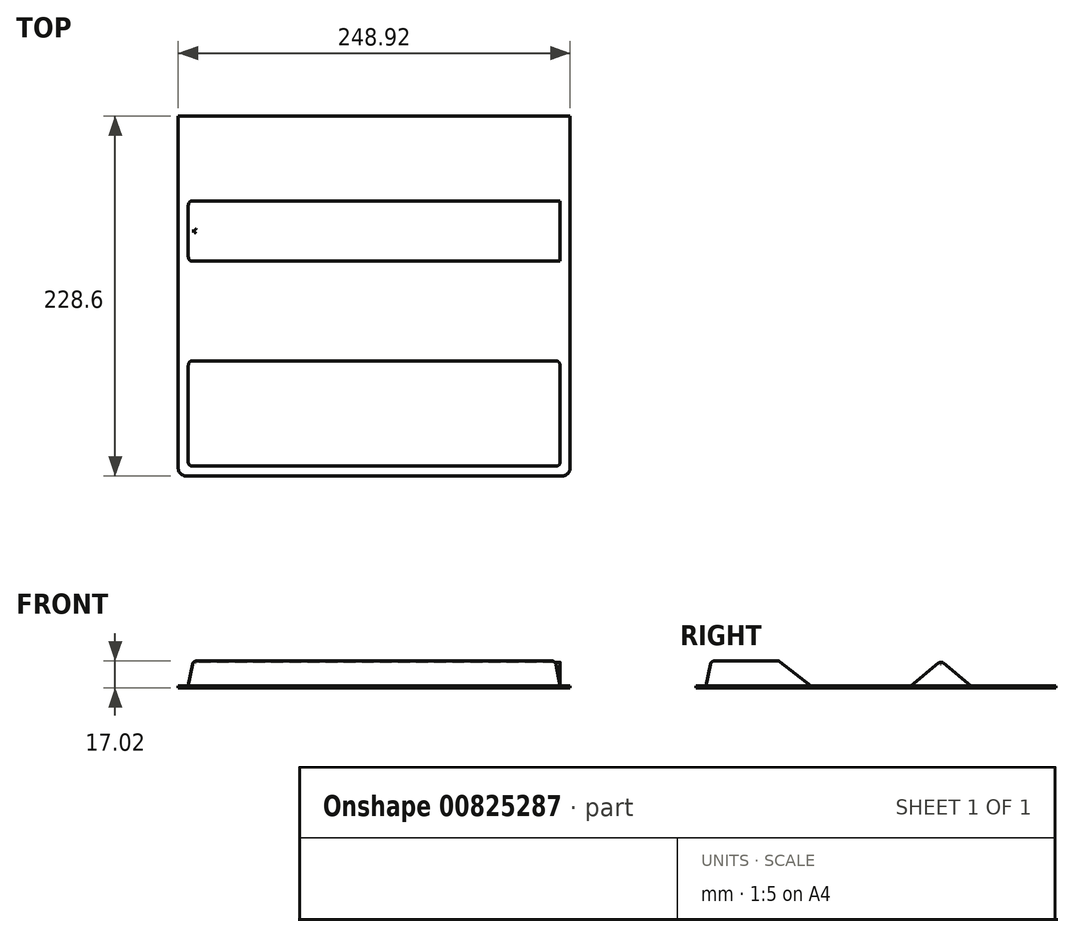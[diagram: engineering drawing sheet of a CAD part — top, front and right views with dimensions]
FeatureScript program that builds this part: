
annotation { "Feature Type Name" : "Feature", "Feature Type Description" : "" }
export const myFeature = defineFeature(function(context is Context, id is Id, definition is map)
    precondition{}
    {
        {
            var Q0;
            Q0=qCreatedBy(makeId("Top.planeOp"),FACE);
            var sketch = newSketch(context, id + "F0", { "sketchPlane" : qUnion([Q0])});
            skLineSegment(sketch, "E0.bottom", {"start": v(-124.46, -114.3) * mm, "end": v(124.46, -114.3) * mm});
            skLineSegment(sketch, "E0.top", {"start": v(-124.46, 114.3) * mm, "end": v(124.46, 114.3) * mm});
            skLineSegment(sketch, "E0.left", {"start": v(-124.46, -114.3) * mm, "end": v(-124.46, 114.3) * mm});
            skLineSegment(sketch, "E0.right", {"start": v(124.46, -114.3) * mm, "end": v(124.46, 114.3) * mm});
            skPoint(sketch, "E0.middle", {"position": v(0, 0) * mm});
            skSolve(sketch);
        }
        {
            var Q0;
            Q0=makeQuery(id+"F0.imprint","IMPRINT",FACE,{"disambiguationData":[TD([[makeQuery(id+"F0.imprint","IMPRINT",EDGE,{"derivedFrom":sQuery(id+"F0.wireOp",EDGE,"E0.bottom")}),1.0]])]});
            extrude(context, id + "F1", {"entities" : qUnion([Q0]), "depth" : 1.27 * mm, "offsetDistance" : 25.4 * mm});
        }
        {
            var Q0;
            Q0=makeQuery(id+"F1.opExtrude","CAP_FACE",FACE,{"disambiguationData":[OSD([sQuery(id+"F0.wireOp",EDGE,"E0.bottom"),sQuery(id+"F0.wireOp",EDGE,"E0.top"),sQuery(id+"F0.wireOp",EDGE,"E0.left"),sQuery(id+"F0.wireOp",EDGE,"E0.right")])],"isStart":false});
            var sketch = newSketch(context, id + "F2", { "sketchPlane" : qUnion([Q0])});
            skLineSegment(sketch, "E1.bottom", {"start": v(118.11, -107.95) * mm, "end": v(-118.11, -107.95) * mm});
            skLineSegment(sketch, "E1.top", {"start": v(118.11, -41.28) * mm, "end": v(-118.11, -41.28) * mm});
            skLineSegment(sketch, "E1.left", {"start": v(118.11, -107.95) * mm, "end": v(118.11, -41.28) * mm});
            skLineSegment(sketch, "E1.right", {"start": v(-118.11, -107.95) * mm, "end": v(-118.11, -41.28) * mm});
            skPoint(sketch, "E1.middle", {"position": v(0, -74.61) * mm});
            skSolve(sketch);
        }
        {
            var Q0;
            Q0=qCreatedBy(makeId("Top.planeOp"),FACE);
            cPlane(context, id + "F3", {"entities" : qUnion([Q0]), "cplaneType" : CPlaneType.OFFSET, "offset" : 17.02 * mm, "width" : 152.4 * mm, "height" : 152.4 * mm});
        }
        {
            var Q0;
            Q0=qCreatedBy(id+"F3.planeOp",FACE);
            var sketch = newSketch(context, id + "F4", { "sketchPlane" : qUnion([Q0])});
            skLineSegment(sketch, "E2.bottom", {"start": v(114.94, -104.78) * mm, "end": v(-114.94, -104.78) * mm});
            skLineSegment(sketch, "E2.top", {"start": v(114.94, -61.6) * mm, "end": v(-114.94, -61.6) * mm});
            skLineSegment(sketch, "E2.left", {"start": v(114.94, -104.78) * mm, "end": v(114.94, -61.6) * mm});
            skLineSegment(sketch, "E2.right", {"start": v(-114.94, -104.78) * mm, "end": v(-114.94, -61.6) * mm});
            skPoint(sketch, "E2.middle", {"position": v(0, -83.19) * mm});
            skSolve(sketch);
        }
        {
            var Q1;
            Q1=makeQuery(id+"F4.imprint","IMPRINT",FACE,{"disambiguationData":[TD([[makeQuery(id+"F4.imprint","IMPRINT",EDGE,{"derivedFrom":sQuery(id+"F4.wireOp",EDGE,"E2.bottom")}),-1.0]])]});
            var Q2;
            Q2=makeQuery(id+"F2.imprint","IMPRINT",FACE,{"disambiguationData":[TD([[makeQuery(id+"F2.imprint","IMPRINT",EDGE,{"derivedFrom":sQuery(id+"F2.wireOp",EDGE,"E1.bottom")}),-1.0]])]});
            loft(context, id + "F5", {"operationType" : NewBodyOperationType.ADD, "sheetProfilesArray" : [{ "sheetProfileEntities" : qUnion([Q1]) }, { "sheetProfileEntities" : qUnion([Q2]) }]});
        }
        {
            var Q0;
            Q0=qCreatedBy(makeId("Right.planeOp"),FACE);
            var sketch = newSketch(context, id + "F6", { "sketchPlane" : qUnion([Q0])});
            skLineSegment(sketch, "E3", {"start": v(22.22, 1.27) * mm, "end": v(60.32, 1.27) * mm});
            skLineSegment(sketch, "E4", {"start": v(60.32, 1.27) * mm, "end": v(41.27, 17.02) * mm});
            skLineSegment(sketch, "E5", {"start": v(41.27, 17.02) * mm, "end": v(22.22, 1.27) * mm});
            skSolve(sketch);
        }
        {
            var Q0;
            Q0=makeQuery(id+"F6.imprint","IMPRINT",FACE,{"disambiguationData":[TD([[makeQuery(id+"F6.imprint","IMPRINT",EDGE,{"derivedFrom":sQuery(id+"F6.wireOp",EDGE,"E3")}),1.0]])]});
            extrude(context, id + "F7", {"entities" : qUnion([Q0]), "operationType" : NewBodyOperationType.ADD, "endBound" : BoundingType.SYMMETRIC, "depth" : 236.22 * mm, "offsetDistance" : 25.4 * mm});
        }
        {
            var Q0;
            Q0=qCreatedBy(id+"F3.planeOp",FACE);
            var sketch = newSketch(context, id + "F8", { "sketchPlane" : qUnion([Q0])});
            skLineSegment(sketch, "E6.left", {"start": v(-114.94, 21.55) * mm, "end": v(-114.94, 60.52) * mm});
            skLineSegment(sketch, "E6.right", {"start": v(-118.25, 21.55) * mm, "end": v(-118.25, 60.52) * mm});
            skLineSegment(sketch, "E7", {"start": v(-118.25, 60.52) * mm, "end": v(-114.94, 60.52) * mm});
            skLineSegment(sketch, "E8", {"start": v(-118.25, 21.55) * mm, "end": v(-114.94, 21.55) * mm});
            skSolve(sketch);
        }
        {
            var Q0;
            Q0=makeQuery(id+"F2.imprint","IMPRINT",FACE,{"disambiguationData":[TD([[makeQuery(id+"F2.imprint","IMPRINT",EDGE,{"derivedFrom":sQuery(id+"F2.wireOp",EDGE,"E1.bottom")}),1.0]])]});
            var sketch = newSketch(context, id + "F9", { "sketchPlane" : qUnion([Q0])});
            skLineSegment(sketch, "E9.bottom", {"start": v(-124.68, 60.59) * mm, "end": v(-118.1, 60.59) * mm});
            skLineSegment(sketch, "E9.top", {"start": v(-124.68, 20.65) * mm, "end": v(-118.1, 20.65) * mm});
            skLineSegment(sketch, "E9.left", {"start": v(-124.68, 60.59) * mm, "end": v(-124.68, 20.65) * mm});
            skLineSegment(sketch, "E9.right", {"start": v(-118.1, 60.59) * mm, "end": v(-118.1, 20.65) * mm});
            skSolve(sketch);
        }
        {
            var Q1;
            Q1 = qSketchRegion(id + "F8", true);
            var Q2;
            Q2 = qSketchRegion(id + "F9", true);
            loft(context, id + "F10", {"operationType" : NewBodyOperationType.REMOVE, "sheetProfilesArray" : [{ "sheetProfileEntities" : qUnion([Q1]) }, { "sheetProfileEntities" : qUnion([Q2]) }]});
        }
        {
            var Q0;
            Q0=makeQuery(id+"F10.boolean.opBoolean","INTERSECT",EDGE,{"derivedFrom":[makeQuery(id+"F7.opExtrude","SWEPT_FACE",FACE,{"disambiguationData":[OSD([sQuery(id+"F6.wireOp",EDGE,"E4")])]}),makeQuery(id+"F10.opLoft","SWEPT_FACE",FACE,{"disambiguationData":[OSD([sQuery(id+"F8.wireOp",EDGE,"E6.left"),sQuery(id+"F8.wireOp",EDGE,"E7"),sQuery(id+"F8.wireOp",EDGE,"E8"),sQuery(id+"F9.wireOp",EDGE,"E9.bottom"),sQuery(id+"F9.wireOp",EDGE,"E9.top"),sQuery(id+"F9.wireOp",EDGE,"E9.right")])]})]});
            var Q1;
            Q1=makeQuery(id+"F10.boolean.opBoolean","INTERSECT",EDGE,{"derivedFrom":[makeQuery(id+"F7.opExtrude","SWEPT_FACE",FACE,{"disambiguationData":[OSD([sQuery(id+"F6.wireOp",EDGE,"E5")])]}),makeQuery(id+"F10.opLoft","SWEPT_FACE",FACE,{"disambiguationData":[OSD([sQuery(id+"F8.wireOp",EDGE,"E6.left"),sQuery(id+"F8.wireOp",EDGE,"E7"),sQuery(id+"F8.wireOp",EDGE,"E8"),sQuery(id+"F9.wireOp",EDGE,"E9.bottom"),sQuery(id+"F9.wireOp",EDGE,"E9.top"),sQuery(id+"F9.wireOp",EDGE,"E9.right")])]})]});
            var Q2;
            Q2=makeQuery(id+"F7.opExtrude","SWEPT_EDGE",EDGE,{"disambiguationData":[OSD([sQuery(id+"F6.wireOp",EDGE,"E4"),sQuery(id+"F6.wireOp",EDGE,"E5")])]});
            var Q3;
            Q3=makeQuery(id+"FepYB7Uw0ol19Tb_1.1.F10.boolean.opBoolean","INTERSECT",EDGE,{"derivedFrom":[makeQuery(id+"F7.opExtrude","SWEPT_FACE",FACE,{"disambiguationData":[OSD([sQuery(id+"F6.wireOp",EDGE,"E4")])]}),makeQuery(id+"FepYB7Uw0ol19Tb_1.1.F10.opLoft","SWEPT_FACE",FACE,{"disambiguationData":[OSD([sQuery(id+"F8.wireOp",EDGE,"E6.left"),sQuery(id+"F8.wireOp",EDGE,"E7"),sQuery(id+"F8.wireOp",EDGE,"E8"),sQuery(id+"F9.wireOp",EDGE,"E9.bottom"),sQuery(id+"F9.wireOp",EDGE,"E9.top"),sQuery(id+"F9.wireOp",EDGE,"E9.right")])]})]});
            var Q4;
            Q4=makeQuery(id+"FepYB7Uw0ol19Tb_1.1.F10.boolean.opBoolean","INTERSECT",EDGE,{"derivedFrom":[makeQuery(id+"F7.opExtrude","SWEPT_FACE",FACE,{"disambiguationData":[OSD([sQuery(id+"F6.wireOp",EDGE,"E5")])]}),makeQuery(id+"FepYB7Uw0ol19Tb_1.1.F10.opLoft","SWEPT_FACE",FACE,{"disambiguationData":[OSD([sQuery(id+"F8.wireOp",EDGE,"E6.left"),sQuery(id+"F8.wireOp",EDGE,"E7"),sQuery(id+"F8.wireOp",EDGE,"E8"),sQuery(id+"F9.wireOp",EDGE,"E9.bottom"),sQuery(id+"F9.wireOp",EDGE,"E9.top"),sQuery(id+"F9.wireOp",EDGE,"E9.right")])]})]});
            var Q5;
            Q5=makeQuery(id+"F5.opLoft","SWEPT_EDGE",EDGE,{"disambiguationData":[OSD([sQuery(id+"F2.wireOp",EDGE,"E1.top"),sQuery(id+"F2.wireOp",EDGE,"E1.right"),sQuery(id+"F4.wireOp",EDGE,"E2.top"),sQuery(id+"F4.wireOp",EDGE,"E2.right")])]});
            var Q6;
            Q6=makeQuery(id+"F5.opLoft","MID_CAP_EDGE",EDGE,{"disambiguationData":[OSD([sQuery(id+"F4.wireOp",EDGE,"E2.top"),sQuery(id+"F4.wireOp",EDGE,"E2.left"),sQuery(id+"F4.wireOp",EDGE,"E2.right")])],"capPos":0.0});
            var Q7;
            Q7=makeQuery(id+"F5.opLoft","SWEPT_EDGE",EDGE,{"disambiguationData":[OSD([sQuery(id+"F2.wireOp",EDGE,"E1.top"),sQuery(id+"F2.wireOp",EDGE,"E1.left"),sQuery(id+"F4.wireOp",EDGE,"E2.top"),sQuery(id+"F4.wireOp",EDGE,"E2.left")])]});
            var Q8;
            Q8=makeQuery(id+"F5.opLoft","MID_CAP_EDGE",EDGE,{"disambiguationData":[OSD([sQuery(id+"F4.wireOp",EDGE,"E2.bottom"),sQuery(id+"F4.wireOp",EDGE,"E2.top"),sQuery(id+"F4.wireOp",EDGE,"E2.left")])],"capPos":0.0});
            var Q9;
            Q9=makeQuery(id+"F5.opLoft","MID_CAP_EDGE",EDGE,{"disambiguationData":[OSD([sQuery(id+"F4.wireOp",EDGE,"E2.bottom"),sQuery(id+"F4.wireOp",EDGE,"E2.top"),sQuery(id+"F4.wireOp",EDGE,"E2.right")])],"capPos":0.0});
            var Q10;
            Q10=makeQuery(id+"F5.opLoft","MID_CAP_EDGE",EDGE,{"disambiguationData":[OSD([sQuery(id+"F4.wireOp",EDGE,"E2.bottom"),sQuery(id+"F4.wireOp",EDGE,"E2.left"),sQuery(id+"F4.wireOp",EDGE,"E2.right")])],"capPos":0.0});
            var Q11;
            Q11=makeQuery(id+"F5.opLoft","SWEPT_EDGE",EDGE,{"disambiguationData":[OSD([sQuery(id+"F2.wireOp",EDGE,"E1.bottom"),sQuery(id+"F2.wireOp",EDGE,"E1.right"),sQuery(id+"F4.wireOp",EDGE,"E2.bottom"),sQuery(id+"F4.wireOp",EDGE,"E2.right")])]});
            var Q12;
            Q12=makeQuery(id+"F5.opLoft","SWEPT_EDGE",EDGE,{"disambiguationData":[OSD([sQuery(id+"F2.wireOp",EDGE,"E1.bottom"),sQuery(id+"F2.wireOp",EDGE,"E1.left"),sQuery(id+"F4.wireOp",EDGE,"E2.bottom"),sQuery(id+"F4.wireOp",EDGE,"E2.left")])]});
            var Q13;
            Q13=makeQuery(id+"F7.opExtrude","SWEPT_EDGE",EDGE,{"disambiguationData":[OSD([sQuery(id+"F6.wireOp",EDGE,"E3"),sQuery(id+"F6.wireOp",EDGE,"E4")])]});
            var Q14;
            Q14=makeQuery(id+"F5.opLoft","MID_CAP_EDGE",EDGE,{"disambiguationData":[OSD([sQuery(id+"F2.wireOp",EDGE,"E1.top"),sQuery(id+"F2.wireOp",EDGE,"E1.left"),sQuery(id+"F2.wireOp",EDGE,"E1.right")])],"capPos":1.0});
            fillet(context, id + "F11", {"entities" : qUnion([Q0, Q1, Q2, Q3, Q4, Q5, Q6, Q7, Q8, Q9, Q10, Q11, Q12, Q13, Q14]), "radius" : 2.54 * mm, "tangentPropagation" : true, "allowEdgeOverflow" : false});
        }
        {
            var Q0;
            Q0=makeQuery(id+"F1.opExtrude","SWEPT_EDGE",EDGE,{"disambiguationData":[OSD([sQuery(id+"F0.wireOp",EDGE,"E0.bottom"),sQuery(id+"F0.wireOp",EDGE,"E0.right")])]});
            var Q1;
            Q1=makeQuery(id+"F1.opExtrude","SWEPT_EDGE",EDGE,{"disambiguationData":[OSD([sQuery(id+"F0.wireOp",EDGE,"E0.bottom"),sQuery(id+"F0.wireOp",EDGE,"E0.left")])]});
            fillet(context, id + "F12", {"entities" : qUnion([Q0, Q1]), "radius" : 5.08 * mm, "tangentPropagation" : true, "allowEdgeOverflow" : false});
        }
    });
